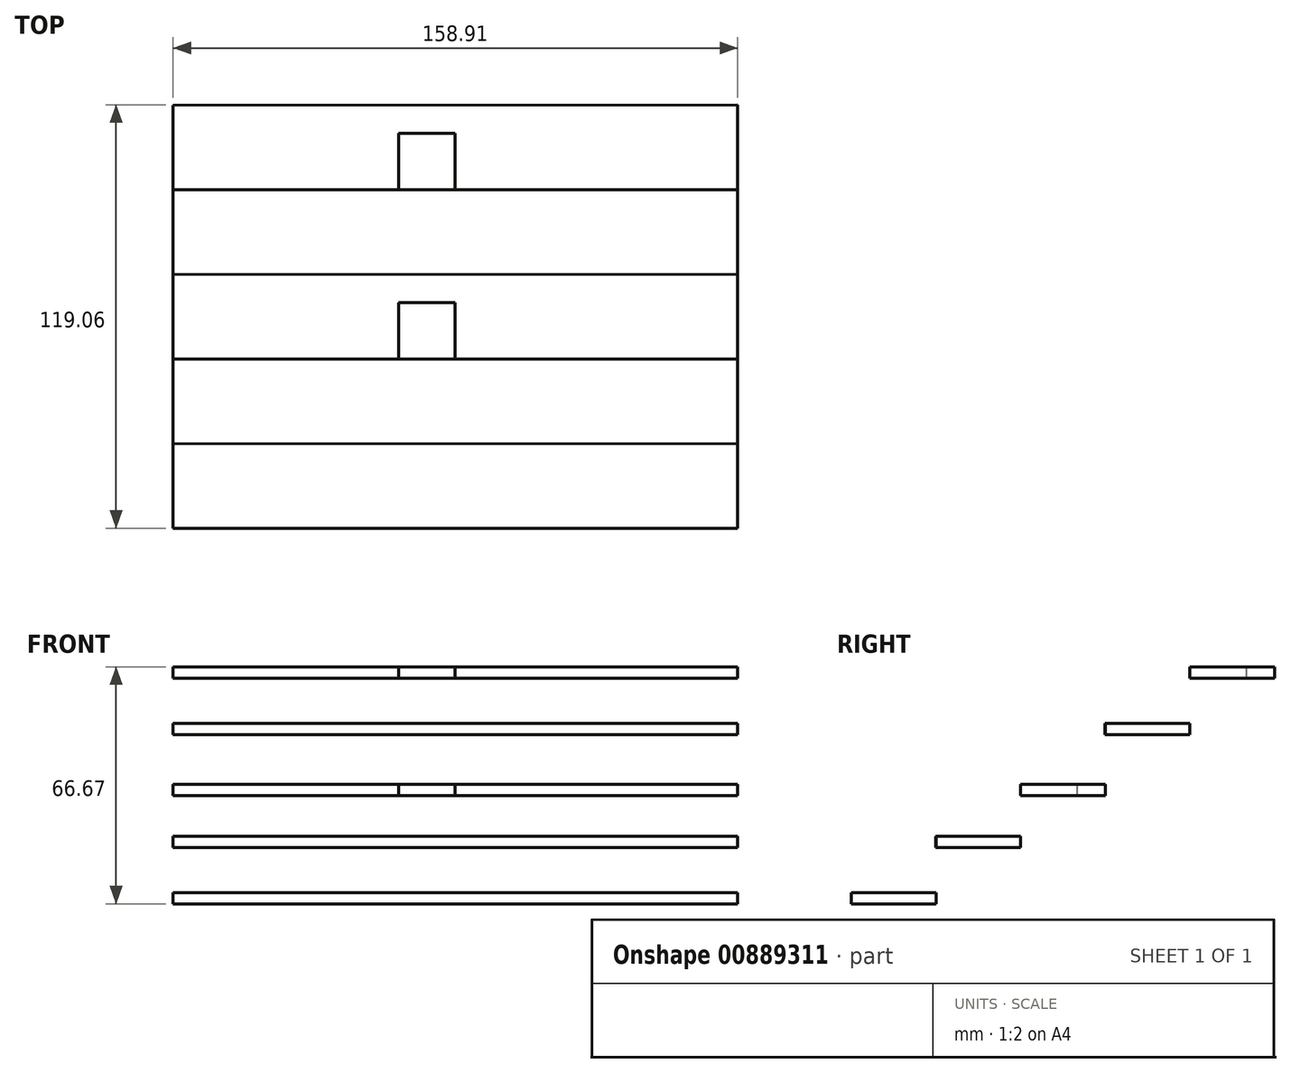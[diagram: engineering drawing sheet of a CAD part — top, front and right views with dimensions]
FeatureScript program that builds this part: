
annotation { "Feature Type Name" : "Feature", "Feature Type Description" : "" }
export const myFeature = defineFeature(function(context is Context, id is Id, definition is map)
    precondition{}
    {
        {
            var Q0;
            Q0=qCreatedBy(makeId("Top.planeOp"),FACE);
            var sketch = newSketch(context, id + "F0", { "sketchPlane" : qUnion([Q0])});
            skLineSegment(sketch, "E0", {"start": v(0, 0) * mm, "end": v(15.88, 0) * mm});
            skLineSegment(sketch, "E1", {"start": v(15.88, 0) * mm, "end": v(15.88, 15.88) * mm});
            skLineSegment(sketch, "E2", {"start": v(15.88, 15.88) * mm, "end": v(0, 15.88) * mm});
            skLineSegment(sketch, "E3", {"start": v(0, 15.88) * mm, "end": v(0, 0) * mm});
            skLineSegment(sketch, "E4.1.0.0", {"start": v(31.75, 0) * mm, "end": v(47.62, 0) * mm});
            skLineSegment(sketch, "E4.1.0.1", {"start": v(31.75, 15.88) * mm, "end": v(31.75, 0) * mm});
            skLineSegment(sketch, "E4.1.0.2", {"start": v(47.62, 0) * mm, "end": v(47.62, 15.88) * mm});
            skLineSegment(sketch, "E4.1.0.3", {"start": v(47.62, 15.88) * mm, "end": v(31.75, 15.88) * mm});
            skLineSegment(sketch, "E4.2.0.0", {"start": v(63.5, 0) * mm, "end": v(79.38, 0) * mm});
            skLineSegment(sketch, "E4.2.0.1", {"start": v(63.5, 15.88) * mm, "end": v(63.5, 0) * mm});
            skLineSegment(sketch, "E4.2.0.2", {"start": v(79.38, 0) * mm, "end": v(79.38, 15.88) * mm});
            skLineSegment(sketch, "E4.2.0.3", {"start": v(79.38, 15.88) * mm, "end": v(63.5, 15.88) * mm});
            skLineSegment(sketch, "E4.3.0.0", {"start": v(95.25, 0) * mm, "end": v(111.12, 0) * mm});
            skLineSegment(sketch, "E4.3.0.1", {"start": v(95.25, 15.88) * mm, "end": v(95.25, 0) * mm});
            skLineSegment(sketch, "E4.3.0.2", {"start": v(111.12, 0) * mm, "end": v(111.12, 15.88) * mm});
            skLineSegment(sketch, "E4.3.0.3", {"start": v(111.12, 15.88) * mm, "end": v(95.25, 15.88) * mm});
            skLineSegment(sketch, "E4.4.0.0", {"start": v(127, 0) * mm, "end": v(142.88, 0) * mm});
            skLineSegment(sketch, "E4.4.0.1", {"start": v(127, 15.88) * mm, "end": v(127, 0) * mm});
            skLineSegment(sketch, "E4.4.0.2", {"start": v(142.88, 0) * mm, "end": v(142.88, 15.88) * mm});
            skLineSegment(sketch, "E4.4.0.3", {"start": v(142.88, 15.88) * mm, "end": v(127, 15.88) * mm});
            skLineSegment(sketch, "E4.direction1", {"start": v(0, 0) * mm, "end": v(31.75, 0) * mm, "construction": true});
            skLineSegment(sketch, "E5.direction1", {"start": v(0, 0) * mm, "end": v(25.4, 0) * mm, "construction": true});
            skLineSegment(sketch, "E5.direction2", {"start": v(0, 0) * mm, "end": v(0, 0) * mm});
            skLineSegment(sketch, "E6.direction1", {"start": v(15.88, 0) * mm, "end": v(31.75, 0) * mm, "construction": true});
            skLineSegment(sketch, "E7", {"start": v(15.88, 23.81) * mm, "end": v(15.88, 39.69) * mm});
            skLineSegment(sketch, "E8", {"start": v(15.88, 39.69) * mm, "end": v(31.8, 39.69) * mm});
            skLineSegment(sketch, "E9", {"start": v(31.8, 39.69) * mm, "end": v(31.8, 23.81) * mm});
            skLineSegment(sketch, "E10", {"start": v(31.8, 23.81) * mm, "end": v(15.88, 23.81) * mm});
            skLineSegment(sketch, "E11.1.0.0", {"start": v(47.62, 23.81) * mm, "end": v(47.62, 39.69) * mm});
            skLineSegment(sketch, "E11.1.0.1", {"start": v(63.55, 39.69) * mm, "end": v(63.55, 23.81) * mm});
            skLineSegment(sketch, "E11.1.0.2", {"start": v(63.55, 23.81) * mm, "end": v(47.62, 23.81) * mm});
            skLineSegment(sketch, "E11.1.0.3", {"start": v(47.62, 39.69) * mm, "end": v(63.55, 39.69) * mm});
            skLineSegment(sketch, "E11.2.0.0", {"start": v(79.38, 23.81) * mm, "end": v(79.38, 39.69) * mm});
            skLineSegment(sketch, "E11.2.0.1", {"start": v(95.3, 39.69) * mm, "end": v(95.3, 23.81) * mm});
            skLineSegment(sketch, "E11.2.0.2", {"start": v(95.3, 23.81) * mm, "end": v(79.37, 23.81) * mm});
            skLineSegment(sketch, "E11.2.0.3", {"start": v(79.37, 39.69) * mm, "end": v(95.3, 39.69) * mm});
            skLineSegment(sketch, "E11.3.0.0", {"start": v(111.12, 23.81) * mm, "end": v(111.12, 39.69) * mm});
            skLineSegment(sketch, "E11.3.0.1", {"start": v(127.05, 39.69) * mm, "end": v(127.05, 23.81) * mm});
            skLineSegment(sketch, "E11.3.0.2", {"start": v(127.05, 23.81) * mm, "end": v(111.12, 23.81) * mm});
            skLineSegment(sketch, "E11.3.0.3", {"start": v(111.12, 39.69) * mm, "end": v(127.05, 39.69) * mm});
            skLineSegment(sketch, "E11.4.0.0", {"start": v(142.88, 23.81) * mm, "end": v(142.88, 39.69) * mm});
            skLineSegment(sketch, "E11.4.0.1", {"start": v(158.8, 39.69) * mm, "end": v(158.8, 23.81) * mm});
            skLineSegment(sketch, "E11.4.0.2", {"start": v(158.8, 23.81) * mm, "end": v(142.87, 23.81) * mm});
            skLineSegment(sketch, "E11.4.0.3", {"start": v(142.87, 39.69) * mm, "end": v(158.8, 39.69) * mm});
            skLineSegment(sketch, "E11.direction1", {"start": v(15.88, 23.81) * mm, "end": v(47.62, 23.81) * mm, "construction": true});
            skLineSegment(sketch, "E12", {"start": v(158.8, 23.81) * mm, "end": v(158.8, 0) * mm});
            skLineSegment(sketch, "E13", {"start": v(158.8, 0) * mm, "end": v(0, 0) * mm});
            skLineSegment(sketch, "E14", {"start": v(-0.01, 23.74) * mm, "end": v(158.8, 23.81) * mm});
            skLineSegment(sketch, "E15", {"start": v(-0.01, 23.74) * mm, "end": v(0, 0) * mm});
            skLineSegment(sketch, "E16", {"start": v(-0.01, 23.74) * mm, "end": v(-0.02, 47.62) * mm});
            skLineSegment(sketch, "E17", {"start": v(-0.02, 47.62) * mm, "end": v(158.89, 47.62) * mm});
            skLineSegment(sketch, "E18", {"start": v(158.89, 47.62) * mm, "end": v(158.8, 23.81) * mm});
            skLineSegment(sketch, "E19.0.1.0", {"start": v(142.88, 71.44) * mm, "end": v(142.88, 87.31) * mm});
            skLineSegment(sketch, "E19.0.1.1", {"start": v(142.88, 47.63) * mm, "end": v(142.88, 63.5) * mm});
            skLineSegment(sketch, "E19.0.1.2", {"start": v(-0.01, 71.37) * mm, "end": v(158.8, 71.44) * mm});
            skLineSegment(sketch, "E19.0.1.3", {"start": v(79.37, 87.31) * mm, "end": v(95.3, 87.31) * mm});
            skLineSegment(sketch, "E19.0.1.4", {"start": v(158.8, 47.63) * mm, "end": v(0, 47.63) * mm});
            skLineSegment(sketch, "E19.0.1.5", {"start": v(15.88, 63.5) * mm, "end": v(0, 63.5) * mm});
            skLineSegment(sketch, "E19.0.1.6", {"start": v(127, 63.5) * mm, "end": v(127, 47.63) * mm});
            skLineSegment(sketch, "E19.0.1.7", {"start": v(63.5, 47.63) * mm, "end": v(79.38, 47.63) * mm});
            skLineSegment(sketch, "E19.0.1.8", {"start": v(15.88, 47.63) * mm, "end": v(15.88, 63.5) * mm});
            skLineSegment(sketch, "E19.0.1.9", {"start": v(111.12, 63.5) * mm, "end": v(95.25, 63.5) * mm});
            skLineSegment(sketch, "E19.0.1.10", {"start": v(0, 63.5) * mm, "end": v(0, 47.63) * mm});
            skLineSegment(sketch, "E19.0.1.11", {"start": v(15.88, 71.44) * mm, "end": v(15.88, 87.31) * mm});
            skLineSegment(sketch, "E19.0.1.12", {"start": v(158.8, 71.44) * mm, "end": v(142.87, 71.44) * mm});
            skLineSegment(sketch, "E19.0.1.13", {"start": v(-0.01, 71.37) * mm, "end": v(0, 47.63) * mm});
            skLineSegment(sketch, "E19.0.1.14", {"start": v(47.62, 87.31) * mm, "end": v(63.55, 87.31) * mm});
            skLineSegment(sketch, "E19.0.1.15", {"start": v(47.62, 71.44) * mm, "end": v(47.62, 87.31) * mm});
            skLineSegment(sketch, "E19.0.1.16", {"start": v(142.87, 87.31) * mm, "end": v(158.8, 87.31) * mm});
            skLineSegment(sketch, "E19.0.1.17", {"start": v(47.62, 47.63) * mm, "end": v(47.62, 63.5) * mm});
            skLineSegment(sketch, "E19.0.1.18", {"start": v(63.55, 87.31) * mm, "end": v(63.55, 71.44) * mm});
            skLineSegment(sketch, "E19.0.1.19", {"start": v(79.38, 63.5) * mm, "end": v(63.5, 63.5) * mm});
            skLineSegment(sketch, "E19.0.1.20", {"start": v(79.38, 71.44) * mm, "end": v(79.38, 87.31) * mm});
            skLineSegment(sketch, "E19.0.1.21", {"start": v(79.38, 47.63) * mm, "end": v(79.38, 63.5) * mm});
            skLineSegment(sketch, "E19.0.1.22", {"start": v(15.88, 87.31) * mm, "end": v(31.8, 87.31) * mm});
            skLineSegment(sketch, "E19.0.1.23", {"start": v(142.88, 63.5) * mm, "end": v(127, 63.5) * mm});
            skLineSegment(sketch, "E19.0.1.24", {"start": v(-0.02, 95.25) * mm, "end": v(158.89, 95.25) * mm});
            skLineSegment(sketch, "E19.0.1.25", {"start": v(95.25, 47.63) * mm, "end": v(111.12, 47.63) * mm});
            skLineSegment(sketch, "E19.0.1.26", {"start": v(31.75, 63.5) * mm, "end": v(31.75, 47.63) * mm});
            skLineSegment(sketch, "E19.0.1.27", {"start": v(111.12, 87.31) * mm, "end": v(127.05, 87.31) * mm});
            skLineSegment(sketch, "E19.0.1.28", {"start": v(127, 47.63) * mm, "end": v(142.88, 47.63) * mm});
            skLineSegment(sketch, "E19.0.1.29", {"start": v(63.5, 63.5) * mm, "end": v(63.5, 47.63) * mm});
            skLineSegment(sketch, "E19.0.1.30", {"start": v(95.25, 63.5) * mm, "end": v(95.25, 47.63) * mm});
            skLineSegment(sketch, "E19.0.1.31", {"start": v(127.05, 71.44) * mm, "end": v(111.12, 71.44) * mm});
            skLineSegment(sketch, "E19.0.1.32", {"start": v(63.55, 71.44) * mm, "end": v(47.62, 71.44) * mm});
            skLineSegment(sketch, "E19.0.1.33", {"start": v(47.62, 63.5) * mm, "end": v(31.75, 63.5) * mm});
            skLineSegment(sketch, "E19.0.1.34", {"start": v(111.12, 71.44) * mm, "end": v(111.12, 87.31) * mm});
            skLineSegment(sketch, "E19.0.1.35", {"start": v(95.3, 71.44) * mm, "end": v(79.37, 71.44) * mm});
            skLineSegment(sketch, "E19.0.1.36", {"start": v(31.8, 87.31) * mm, "end": v(31.8, 71.44) * mm});
            skLineSegment(sketch, "E19.0.1.37", {"start": v(111.12, 47.63) * mm, "end": v(111.12, 63.5) * mm});
            skLineSegment(sketch, "E19.0.1.38", {"start": v(31.8, 71.44) * mm, "end": v(15.88, 71.44) * mm});
            skLineSegment(sketch, "E19.0.1.39", {"start": v(127.05, 87.31) * mm, "end": v(127.05, 71.44) * mm});
            skLineSegment(sketch, "E19.0.1.40", {"start": v(-0.01, 71.37) * mm, "end": v(-0.02, 95.25) * mm});
            skLineSegment(sketch, "E19.0.1.41", {"start": v(95.3, 87.31) * mm, "end": v(95.3, 71.44) * mm});
            skLineSegment(sketch, "E19.0.1.42", {"start": v(158.89, 95.25) * mm, "end": v(158.8, 71.44) * mm});
            skLineSegment(sketch, "E19.0.1.43", {"start": v(158.8, 71.44) * mm, "end": v(158.8, 47.63) * mm});
            skLineSegment(sketch, "E19.0.1.44", {"start": v(0, 47.63) * mm, "end": v(15.88, 47.63) * mm});
            skLineSegment(sketch, "E19.0.1.45", {"start": v(15.88, 71.44) * mm, "end": v(47.62, 71.44) * mm, "construction": true});
            skLineSegment(sketch, "E19.0.1.46", {"start": v(0, 47.63) * mm, "end": v(25.4, 47.63) * mm, "construction": true});
            skLineSegment(sketch, "E19.0.1.47", {"start": v(0, 47.63) * mm, "end": v(31.75, 47.63) * mm, "construction": true});
            skLineSegment(sketch, "E19.0.1.48", {"start": v(158.8, 87.31) * mm, "end": v(158.8, 71.44) * mm});
            skLineSegment(sketch, "E19.0.1.49", {"start": v(31.75, 47.63) * mm, "end": v(47.62, 47.63) * mm});
            skLineSegment(sketch, "E19.0.1.50", {"start": v(15.88, 47.63) * mm, "end": v(31.75, 47.63) * mm, "construction": true});
            skLineSegment(sketch, "E19.direction2", {"start": v(0, 0) * mm, "end": v(0, 47.63) * mm, "construction": true});
            skLineSegment(sketch, "E20.3.0.2", {"start": v(142.88, 95.25) * mm, "end": v(142.88, 111.12) * mm});
            skLineSegment(sketch, "E20.6.0.2", {"start": v(-0.01, 119) * mm, "end": v(158.8, 119.06) * mm});
            skLineSegment(sketch, "E20.12.0.2", {"start": v(158.8, 95.25) * mm, "end": v(0, 95.25) * mm});
            skLineSegment(sketch, "E20.15.0.2", {"start": v(15.88, 111.12) * mm, "end": v(0, 111.12) * mm});
            skLineSegment(sketch, "E20.18.0.2", {"start": v(127, 111.12) * mm, "end": v(127, 95.25) * mm});
            skLineSegment(sketch, "E20.21.0.2", {"start": v(63.5, 95.25) * mm, "end": v(79.38, 95.25) * mm});
            skLineSegment(sketch, "E20.24.0.2", {"start": v(15.88, 95.25) * mm, "end": v(15.88, 111.12) * mm});
            skLineSegment(sketch, "E20.27.0.2", {"start": v(111.12, 111.12) * mm, "end": v(95.25, 111.12) * mm});
            skLineSegment(sketch, "E20.30.0.2", {"start": v(0, 111.12) * mm, "end": v(0, 95.25) * mm});
            skLineSegment(sketch, "E20.39.0.2", {"start": v(-0.01, 119) * mm, "end": v(0, 95.25) * mm});
            skLineSegment(sketch, "E20.51.0.2", {"start": v(47.62, 95.25) * mm, "end": v(47.62, 111.12) * mm});
            skLineSegment(sketch, "E20.57.0.2", {"start": v(79.38, 111.12) * mm, "end": v(63.5, 111.12) * mm});
            skLineSegment(sketch, "E20.63.0.2", {"start": v(79.38, 95.25) * mm, "end": v(79.38, 111.12) * mm});
            skLineSegment(sketch, "E20.69.0.2", {"start": v(142.88, 111.12) * mm, "end": v(127, 111.12) * mm});
            skLineSegment(sketch, "E20.75.0.2", {"start": v(95.25, 95.25) * mm, "end": v(111.12, 95.25) * mm});
            skLineSegment(sketch, "E20.78.0.2", {"start": v(31.75, 111.12) * mm, "end": v(31.75, 95.25) * mm});
            skLineSegment(sketch, "E20.84.0.2", {"start": v(127, 95.25) * mm, "end": v(142.88, 95.25) * mm});
            skLineSegment(sketch, "E20.87.0.2", {"start": v(63.5, 111.12) * mm, "end": v(63.5, 95.25) * mm});
            skLineSegment(sketch, "E20.90.0.2", {"start": v(95.25, 111.12) * mm, "end": v(95.25, 95.25) * mm});
            skLineSegment(sketch, "E20.99.0.2", {"start": v(47.62, 111.12) * mm, "end": v(31.75, 111.12) * mm});
            skLineSegment(sketch, "E20.111.0.2", {"start": v(111.12, 95.25) * mm, "end": v(111.12, 111.12) * mm});
            skLineSegment(sketch, "E20.129.0.2", {"start": v(158.8, 119.06) * mm, "end": v(158.8, 95.25) * mm});
            skLineSegment(sketch, "E20.132.0.2", {"start": v(0, 95.25) * mm, "end": v(15.88, 95.25) * mm});
            skLineSegment(sketch, "E20.138.0.2", {"start": v(0, 95.25) * mm, "end": v(25.4, 95.25) * mm, "construction": true});
            skLineSegment(sketch, "E20.141.0.2", {"start": v(0, 95.25) * mm, "end": v(31.75, 95.25) * mm, "construction": true});
            skLineSegment(sketch, "E20.147.0.2", {"start": v(31.75, 95.25) * mm, "end": v(47.62, 95.25) * mm});
            skLineSegment(sketch, "E20.150.0.2", {"start": v(15.88, 95.25) * mm, "end": v(31.75, 95.25) * mm, "construction": true});
            skSolve(sketch);
        }
        {
            var Q0;
            {var subQ1=sQuery(id+"F0.wireOp",EDGE,"E1");Q0=makeQuery(id+"F0.imprint","IMPRINT",FACE,{"disambiguationData":[TD([[makeQuery(id+"F0.imprint","IMPRINT",EDGE,{"derivedFrom":subQ1}),-1.0]])]});}
            var Q1;
            {var subQ0=sQuery(id+"F0.wireOp",EDGE,"E1");Q1=makeQuery(id+"F0.imprint","IMPRINT",FACE,{"disambiguationData":[TD([[makeQuery(id+"F0.imprint","IMPRINT",EDGE,{"derivedFrom":subQ0}),1.0]])]});}
            var Q2;
            {var subQ0=sQuery(id+"F0.wireOp",EDGE,"E4.1.0.1");Q2=makeQuery(id+"F0.imprint","IMPRINT",FACE,{"disambiguationData":[TD([[makeQuery(id+"F0.imprint","IMPRINT",EDGE,{"derivedFrom":subQ0}),1.0]])]});}
            var Q3;
            {var subQ0=sQuery(id+"F0.wireOp",EDGE,"E4.2.0.1");Q3=makeQuery(id+"F0.imprint","IMPRINT",FACE,{"disambiguationData":[TD([[makeQuery(id+"F0.imprint","IMPRINT",EDGE,{"derivedFrom":subQ0}),1.0]])]});}
            var Q4;
            {var subQ0=sQuery(id+"F0.wireOp",EDGE,"E4.3.0.1");Q4=makeQuery(id+"F0.imprint","IMPRINT",FACE,{"disambiguationData":[TD([[makeQuery(id+"F0.imprint","IMPRINT",EDGE,{"derivedFrom":subQ0}),1.0]])]});}
            var Q5;
            {var subQ0=sQuery(id+"F0.wireOp",EDGE,"E4.4.0.1");Q5=makeQuery(id+"F0.imprint","IMPRINT",FACE,{"disambiguationData":[TD([[makeQuery(id+"F0.imprint","IMPRINT",EDGE,{"derivedFrom":subQ0}),1.0]])]});}
            extrude(context, id + "F1", {"entities" : qUnion([Q0, Q1, Q2, Q3, Q4, Q5]), "depth" : 3.17 * mm, "offsetDistance" : 25.4 * mm});
        }
        {
            var Q0;
            Q0=makeQuery(id+"F0.imprint","IMPRINT",FACE,{"disambiguationData":[TD([[makeQuery(id+"F0.imprint","IMPRINT",EDGE,{"derivedFrom":sQuery(id+"F0.wireOp",EDGE,"E7")}),1.0]])]});
            var Q1;
            Q1=makeQuery(id+"F0.imprint","IMPRINT",FACE,{"disambiguationData":[TD([[makeQuery(id+"F0.imprint","IMPRINT",EDGE,{"derivedFrom":sQuery(id+"F0.wireOp",EDGE,"E7")}),-1.0]])]});
            var Q2;
            Q2=makeQuery(id+"F0.imprint","IMPRINT",FACE,{"disambiguationData":[TD([[makeQuery(id+"F0.imprint","IMPRINT",EDGE,{"derivedFrom":sQuery(id+"F0.wireOp",EDGE,"E11.1.0.0")}),-1.0]])]});
            var Q3;
            Q3=makeQuery(id+"F0.imprint","IMPRINT",FACE,{"disambiguationData":[TD([[makeQuery(id+"F0.imprint","IMPRINT",EDGE,{"derivedFrom":sQuery(id+"F0.wireOp",EDGE,"E11.2.0.0")}),-1.0]])]});
            var Q4;
            Q4=makeQuery(id+"F0.imprint","IMPRINT",FACE,{"disambiguationData":[TD([[makeQuery(id+"F0.imprint","IMPRINT",EDGE,{"derivedFrom":sQuery(id+"F0.wireOp",EDGE,"E11.3.0.0")}),-1.0]])]});
            var Q5;
            Q5=makeQuery(id+"F0.imprint","IMPRINT",FACE,{"disambiguationData":[TD([[makeQuery(id+"F0.imprint","IMPRINT",EDGE,{"derivedFrom":sQuery(id+"F0.wireOp",EDGE,"E11.4.0.0")}),-1.0]])]});
            extrude(context, id + "F2", {"entities" : qUnion([Q0, Q1, Q2, Q3, Q4, Q5]), "operationType" : NewBodyOperationType.ADD, "depth" : 19.05 * mm, "offsetDistance" : 25.4 * mm, "hasSecondDirection" : true, "secondDirectionOppositeDirection" : false, "secondDirectionDepth" : 15.88 * mm});
        }
        {
            var Q0;
            {var subQ10=sQuery(id+"F0.wireOp",EDGE,"E19.0.1.1");Q0=makeQuery(id+"F0.imprint","IMPRINT",FACE,{"disambiguationData":[TD([[makeQuery(id+"F0.imprint","IMPRINT",EDGE,{"derivedFrom":subQ10}),-1.0]])]});}
            var Q1;
            Q1=makeQuery(id+"F0.imprint","IMPRINT",FACE,{"disambiguationData":[TD([[makeQuery(id+"F0.imprint","IMPRINT",EDGE,{"derivedFrom":sQuery(id+"F0.wireOp",EDGE,"E19.0.1.5")}),1.0]])]});
            var Q2;
            Q2=makeQuery(id+"F0.imprint","IMPRINT",FACE,{"disambiguationData":[TD([[makeQuery(id+"F0.imprint","IMPRINT",EDGE,{"derivedFrom":sQuery(id+"F0.wireOp",EDGE,"E19.0.1.17")}),1.0]])]});
            var Q3;
            Q3=makeQuery(id+"F0.imprint","IMPRINT",FACE,{"disambiguationData":[TD([[makeQuery(id+"F0.imprint","IMPRINT",EDGE,{"derivedFrom":sQuery(id+"F0.wireOp",EDGE,"E19.0.1.7")}),1.0]])]});
            var Q4;
            Q4=makeQuery(id+"F0.imprint","IMPRINT",FACE,{"disambiguationData":[TD([[makeQuery(id+"F0.imprint","IMPRINT",EDGE,{"derivedFrom":sQuery(id+"F0.wireOp",EDGE,"E19.0.1.9")}),1.0]])]});
            var Q5;
            Q5=makeQuery(id+"F0.imprint","IMPRINT",FACE,{"disambiguationData":[TD([[makeQuery(id+"F0.imprint","IMPRINT",EDGE,{"derivedFrom":sQuery(id+"F0.wireOp",EDGE,"E19.0.1.1")}),1.0]])]});
            extrude(context, id + "F3", {"entities" : qUnion([Q0, Q1, Q2, Q3, Q4, Q5]), "operationType" : NewBodyOperationType.ADD, "depth" : 33.65 * mm, "offsetDistance" : 25.4 * mm, "hasSecondDirection" : true, "secondDirectionOppositeDirection" : false, "secondDirectionDepth" : 30.48 * mm});
        }
        {
            var Q0;
            Q0=makeQuery(id+"F0.imprint","IMPRINT",FACE,{"disambiguationData":[TD([[makeQuery(id+"F0.imprint","IMPRINT",EDGE,{"derivedFrom":sQuery(id+"F0.wireOp",EDGE,"E19.0.1.0")}),1.0]])]});
            var Q1;
            Q1=makeQuery(id+"F0.imprint","IMPRINT",FACE,{"disambiguationData":[TD([[makeQuery(id+"F0.imprint","IMPRINT",EDGE,{"derivedFrom":sQuery(id+"F0.wireOp",EDGE,"E19.0.1.11")}),-1.0]])]});
            var Q2;
            Q2=makeQuery(id+"F0.imprint","IMPRINT",FACE,{"disambiguationData":[TD([[makeQuery(id+"F0.imprint","IMPRINT",EDGE,{"derivedFrom":sQuery(id+"F0.wireOp",EDGE,"E19.0.1.14")}),-1.0]])]});
            var Q3;
            Q3=makeQuery(id+"F0.imprint","IMPRINT",FACE,{"disambiguationData":[TD([[makeQuery(id+"F0.imprint","IMPRINT",EDGE,{"derivedFrom":sQuery(id+"F0.wireOp",EDGE,"E19.0.1.3")}),-1.0]])]});
            var Q4;
            Q4=makeQuery(id+"F0.imprint","IMPRINT",FACE,{"disambiguationData":[TD([[makeQuery(id+"F0.imprint","IMPRINT",EDGE,{"derivedFrom":sQuery(id+"F0.wireOp",EDGE,"E19.0.1.27")}),-1.0]])]});
            var Q5;
            Q5=makeQuery(id+"F0.imprint","IMPRINT",FACE,{"disambiguationData":[TD([[makeQuery(id+"F0.imprint","IMPRINT",EDGE,{"derivedFrom":sQuery(id+"F0.wireOp",EDGE,"E19.0.1.0")}),-1.0]])]});
            extrude(context, id + "F4", {"entities" : qUnion([Q0, Q1, Q2, Q3, Q4, Q5]), "operationType" : NewBodyOperationType.ADD, "depth" : 50.8 * mm, "offsetDistance" : 25.4 * mm, "hasSecondDirection" : true, "secondDirectionOppositeDirection" : false, "secondDirectionDepth" : 47.62 * mm});
        }
        {
            var Q0;
            Q0=makeQuery(id+"F0.imprint","IMPRINT",FACE,{"disambiguationData":[TD([[makeQuery(id+"F0.imprint","IMPRINT",EDGE,{"derivedFrom":sQuery(id+"F0.wireOp",EDGE,"E20.15.0.2")}),1.0]])]});
            var Q1;
            {var subQ11=sQuery(id+"F0.wireOp",EDGE,"E20.3.0.2");Q1=makeQuery(id+"F0.imprint","IMPRINT",FACE,{"disambiguationData":[TD([[makeQuery(id+"F0.imprint","IMPRINT",EDGE,{"derivedFrom":subQ11}),-1.0]])]});}
            var Q2;
            Q2=makeQuery(id+"F0.imprint","IMPRINT",FACE,{"disambiguationData":[TD([[makeQuery(id+"F0.imprint","IMPRINT",EDGE,{"derivedFrom":sQuery(id+"F0.wireOp",EDGE,"E20.51.0.2")}),1.0]])]});
            var Q3;
            Q3=makeQuery(id+"F0.imprint","IMPRINT",FACE,{"disambiguationData":[TD([[makeQuery(id+"F0.imprint","IMPRINT",EDGE,{"derivedFrom":sQuery(id+"F0.wireOp",EDGE,"E20.21.0.2")}),1.0]])]});
            var Q4;
            Q4=makeQuery(id+"F0.imprint","IMPRINT",FACE,{"disambiguationData":[TD([[makeQuery(id+"F0.imprint","IMPRINT",EDGE,{"derivedFrom":sQuery(id+"F0.wireOp",EDGE,"E20.27.0.2")}),1.0]])]});
            var Q5;
            Q5=makeQuery(id+"F0.imprint","IMPRINT",FACE,{"disambiguationData":[TD([[makeQuery(id+"F0.imprint","IMPRINT",EDGE,{"derivedFrom":sQuery(id+"F0.wireOp",EDGE,"E20.3.0.2")}),1.0]])]});
            extrude(context, id + "F5", {"entities" : qUnion([Q0, Q1, Q2, Q3, Q4, Q5]), "operationType" : NewBodyOperationType.ADD, "depth" : 66.67 * mm, "offsetDistance" : 25.4 * mm, "hasSecondDirection" : true, "secondDirectionOppositeDirection" : false, "secondDirectionDepth" : 63.5 * mm});
        }
    });
